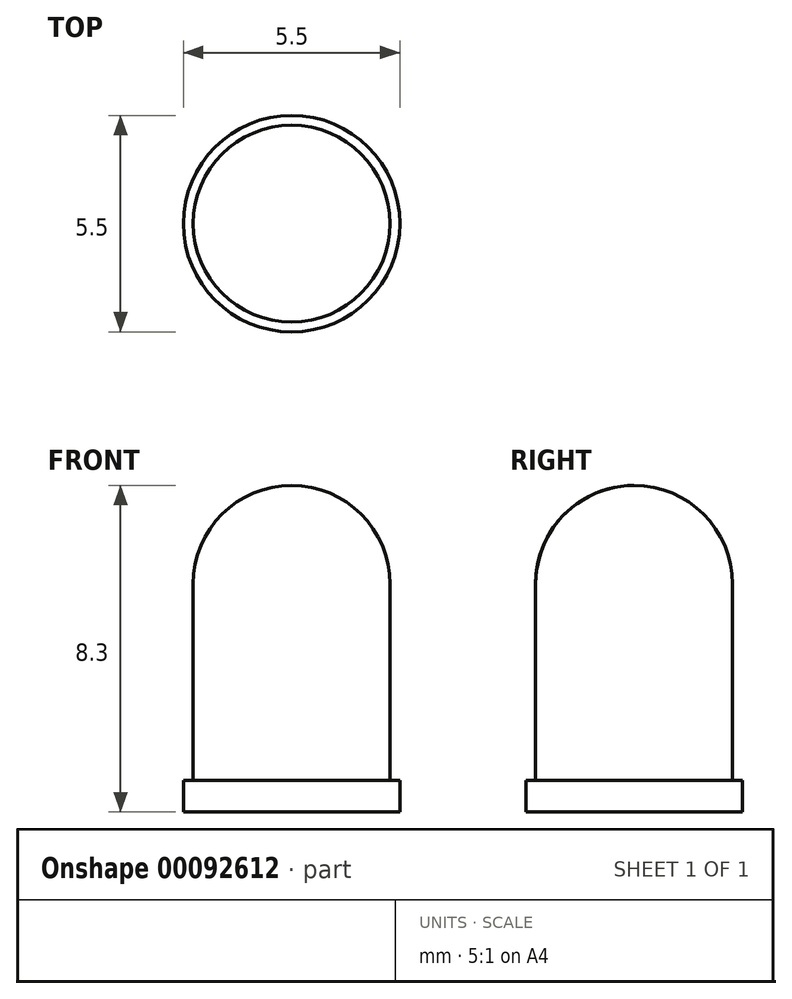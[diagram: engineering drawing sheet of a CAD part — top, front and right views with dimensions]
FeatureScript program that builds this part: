
annotation { "Feature Type Name" : "Feature", "Feature Type Description" : "" }
export const myFeature = defineFeature(function(context is Context, id is Id, definition is map)
    precondition{}
    {
        {
            var Q0;
            Q0=qCreatedBy(makeId("Top.planeOp"),FACE);
            var sketch = newSketch(context, id + "F0", { "sketchPlane" : qUnion([Q0])});
            skCircle(sketch, "E0", {"center": v(0, 0) * mm, "radius": 2.75 * mm});
            skSolve(sketch);
        }
        {
            var Q0;
            Q0 = qSketchRegion(id + "F0", true);
            extrude(context, id + "F1", {"entities" : qUnion([Q0]), "depth" : 0.8 * mm});
        }
        {
            var Q0;
            Q0=qCreatedBy(makeId("Right.planeOp"),FACE);
            var sketch = newSketch(context, id + "F2", { "sketchPlane" : qUnion([Q0])});
            skLineSegment(sketch, "E1", {"start": v(0, 0) * mm, "end": v(0, 8.3) * mm});
            skLineSegment(sketch, "E2", {"start": v(-2.5, 5.8) * mm, "end": v(-2.5, 0) * mm});
            skLineSegment(sketch, "E3", {"start": v(-2.5, 0) * mm, "end": v(0, 0) * mm});
            skArc(sketch, "E4", {"start": v(0, 8.3) * mm, "mid": v(-1.77, 7.57) * mm, "end": v(-2.5, 5.8) * mm});
            skLineSegment(sketch, "E5", {"start": v(3.3, 5.8) * mm, "end": v(-6.6, 5.8) * mm, "construction": true});
            skSolve(sketch);
        }
        {
            var Q0;
            Q0 = qSketchRegion(id + "F2", true);
            var Q1;
            Q1=sQuery(id+"F2.wireOp",EDGE,"E1");
            revolve(context, id + "F3", {"operationType" : NewBodyOperationType.ADD, "entities" : qUnion([Q0]), "axis" : qUnion([Q1]), "revolveType" : RevolveType.FULL});
        }
    });
